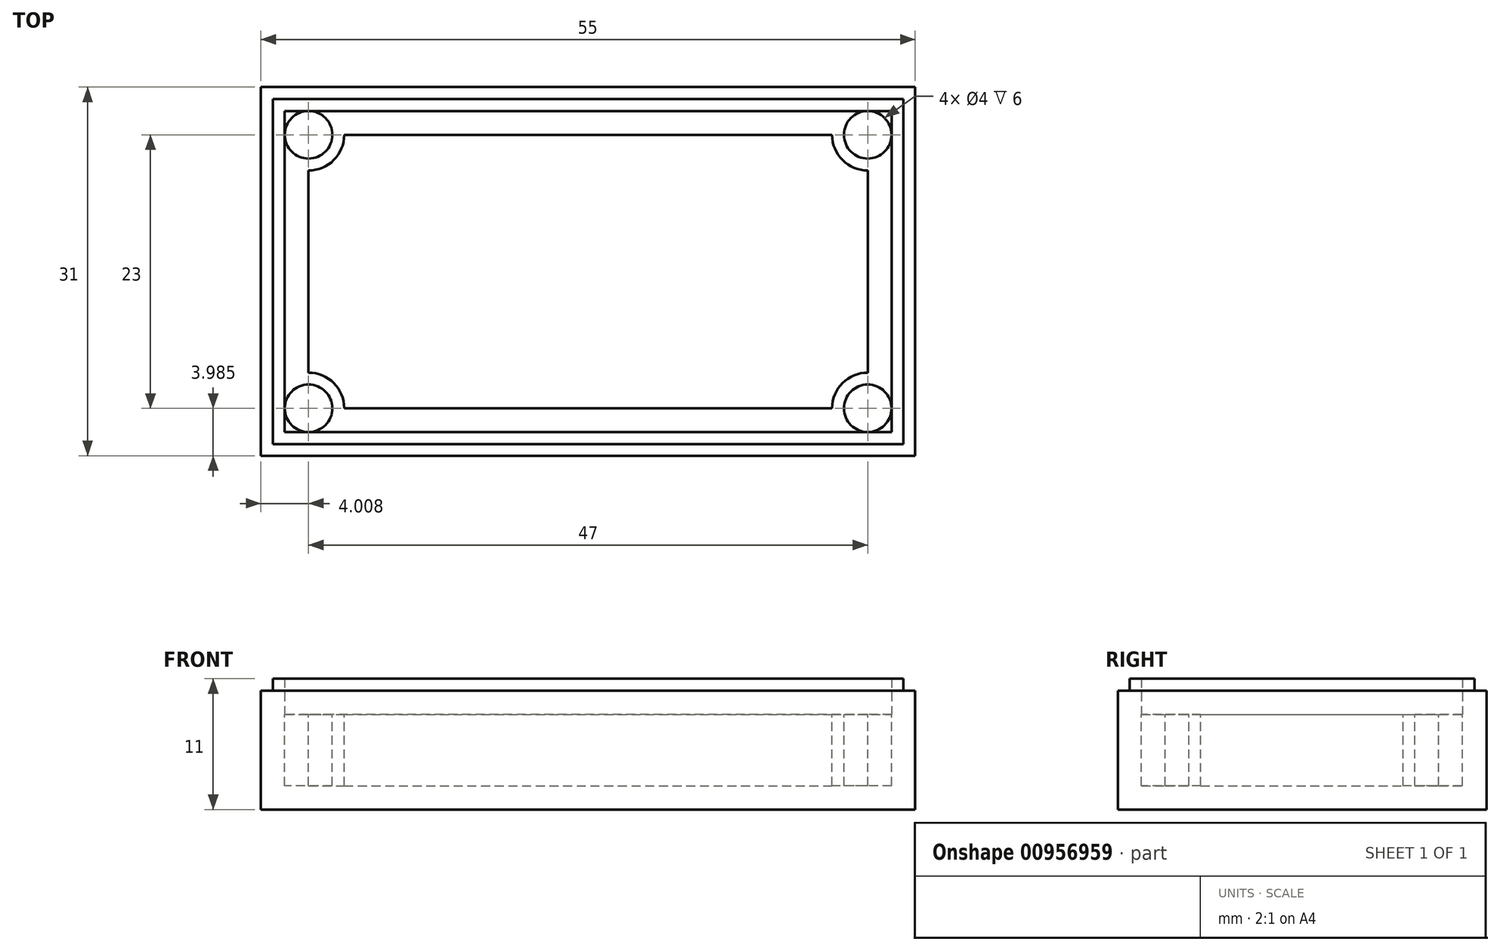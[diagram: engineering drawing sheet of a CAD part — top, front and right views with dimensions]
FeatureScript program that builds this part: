
annotation { "Feature Type Name" : "Feature", "Feature Type Description" : "" }
export const myFeature = defineFeature(function(context is Context, id is Id, definition is map)
    precondition{}
    {
        {
            var Q0;
            Q0=qCreatedBy(makeId("Top.planeOp"),FACE);
            var sketch = newSketch(context, id + "F0", { "sketchPlane" : qUnion([Q0])});
            skLineSegment(sketch, "E0.bottom", {"start": v(-24.52, 16.7) * mm, "end": v(30.48, 16.7) * mm});
            skLineSegment(sketch, "E0.top", {"start": v(-24.52, -14.3) * mm, "end": v(30.48, -14.3) * mm});
            skLineSegment(sketch, "E0.left", {"start": v(-24.52, 16.7) * mm, "end": v(-24.52, -14.3) * mm});
            skLineSegment(sketch, "E0.right", {"start": v(30.48, 16.7) * mm, "end": v(30.48, -14.3) * mm});
            skSolve(sketch);
        }
        {
            var Q0;
            Q0=makeQuery(id+"F0.imprint","IMPRINT",FACE,{"disambiguationData":[TD([[makeQuery(id+"F0.imprint","IMPRINT",EDGE,{"derivedFrom":sQuery(id+"F0.wireOp",EDGE,"E0.bottom")}),-1.0]])]});
            var sketch = newSketch(context, id + "F1", { "sketchPlane" : qUnion([Q0])});
            skLineSegment(sketch, "E1", {"start": v(-24.51, 15.7) * mm, "end": v(-23.51, 15.7) * mm});
            skLineSegment(sketch, "E2.bottom", {"start": v(-23.51, 15.7) * mm, "end": v(29.49, 15.7) * mm});
            skLineSegment(sketch, "E2.top", {"start": v(-23.51, -13.3) * mm, "end": v(29.49, -13.3) * mm});
            skLineSegment(sketch, "E2.left", {"start": v(-23.51, 15.7) * mm, "end": v(-23.51, -13.3) * mm});
            skLineSegment(sketch, "E2.right", {"start": v(29.49, 15.7) * mm, "end": v(29.49, -13.3) * mm});
            skLineSegment(sketch, "E3", {"start": v(-22.51, 15.7) * mm, "end": v(-22.51, 14.7) * mm});
            skLineSegment(sketch, "E4.bottom", {"start": v(-22.51, 14.7) * mm, "end": v(28.49, 14.7) * mm});
            skLineSegment(sketch, "E4.top", {"start": v(-22.51, -12.3) * mm, "end": v(28.49, -12.3) * mm});
            skLineSegment(sketch, "E4.left", {"start": v(-22.51, 14.7) * mm, "end": v(-22.51, -12.3) * mm});
            skLineSegment(sketch, "E4.right", {"start": v(28.49, 14.7) * mm, "end": v(28.49, -12.3) * mm});
            skSolve(sketch);
        }
        {
            var Q0;
            Q0 = qSketchRegion(id + "F0", true);
            extrude(context, id + "F2", {"entities" : qUnion([Q0]), "depth" : 10 * mm, "offsetDistance" : 25 * mm});
        }
        {
            var Q0;
            Q0=makeQuery(id+"F1.imprint","IMPRINT",FACE,{"disambiguationData":[TD([[makeQuery(id+"F1.imprint","IMPRINT",EDGE,{"derivedFrom":sQuery(id+"F1.wireOp",EDGE,"E2.top")}),1.0]])]});
            extrude(context, id + "F3", {"entities" : qUnion([Q0]), "operationType" : NewBodyOperationType.ADD, "depth" : 11 * mm, "offsetDistance" : 25 * mm});
        }
        {
            var Q0;
            Q0=makeQuery(id+"F3.boolean.opBoolean","SPLIT",FACE,{"disambiguationData":[TD([makeQuery(id+"F3.opExtrude","SWEPT_FACE",FACE,{"disambiguationData":[OSD([sQuery(id+"F1.wireOp",EDGE,"E4.bottom")])]})])],"derivedFrom":makeQuery(id+"F2.opExtrude","CAP_FACE",FACE,{"disambiguationData":[OSD([sQuery(id+"F0.wireOp",EDGE,"E0.bottom"),sQuery(id+"F0.wireOp",EDGE,"E0.top"),sQuery(id+"F0.wireOp",EDGE,"E0.left"),sQuery(id+"F0.wireOp",EDGE,"E0.right")])],"isStart":false})});
            extrude(context, id + "F4", {"entities" : qUnion([Q0]), "operationType" : NewBodyOperationType.REMOVE, "oppositeDirection" : true, "depth" : 8 * mm, "offsetDistance" : 25 * mm});
        }
        {
            var Q0;
            Q0=makeQuery(id+"F4.boolean.opBoolean","COPY",FACE,{"derivedFrom":makeQuery(id+"F4.opExtrude","CAP_FACE",FACE,{"disambiguationData":[OSD([sQuery(id+"F0.wireOp",EDGE,"E0.bottom"),sQuery(id+"F0.wireOp",EDGE,"E0.top"),sQuery(id+"F0.wireOp",EDGE,"E0.left"),sQuery(id+"F0.wireOp",EDGE,"E0.right")])],"isStart":false})});
            var sketch = newSketch(context, id + "F5", { "sketchPlane" : qUnion([Q0])});
            skLineSegment(sketch, "E5.bottom", {"start": v(-22.51, 14.7) * mm, "end": v(28.49, 14.7) * mm});
            skLineSegment(sketch, "E5.top", {"start": v(-22.51, 12.7) * mm, "end": v(28.49, 12.7) * mm});
            skLineSegment(sketch, "E5.left", {"start": v(-22.51, 14.7) * mm, "end": v(-22.51, 12.7) * mm});
            skLineSegment(sketch, "E5.right", {"start": v(28.49, 14.7) * mm, "end": v(28.49, 12.7) * mm});
            skLineSegment(sketch, "E6.bottom", {"start": v(-22.51, -12.3) * mm, "end": v(28.49, -12.3) * mm});
            skLineSegment(sketch, "E6.top", {"start": v(-22.51, -10.3) * mm, "end": v(28.49, -10.3) * mm});
            skLineSegment(sketch, "E6.left", {"start": v(-22.51, -12.3) * mm, "end": v(-22.51, -10.3) * mm});
            skLineSegment(sketch, "E6.right", {"start": v(28.49, -12.3) * mm, "end": v(28.49, -10.3) * mm});
            skSolve(sketch);
        }
        {
            var Q0;
            Q0=makeQuery(id+"F5.imprint","IMPRINT",FACE,{"disambiguationData":[TD([[makeQuery(id+"F5.imprint","IMPRINT",EDGE,{"derivedFrom":sQuery(id+"F5.wireOp",EDGE,"E5.bottom")}),1.0]])]});
            var Q1;
            Q1=makeQuery(id+"F5.imprint","IMPRINT",FACE,{"disambiguationData":[TD([[makeQuery(id+"F5.imprint","IMPRINT",EDGE,{"derivedFrom":sQuery(id+"F5.wireOp",EDGE,"E6.bottom")}),-1.0]])]});
            extrude(context, id + "F6", {"entities" : qUnion([Q0, Q1]), "operationType" : NewBodyOperationType.ADD, "depth" : 6 * mm, "offsetDistance" : 25 * mm});
        }
        {
            var Q0;
            Q0=makeQuery(id+"F4.boolean.opBoolean","COPY",FACE,{"derivedFrom":makeQuery(id+"F4.opExtrude","CAP_FACE",FACE,{"disambiguationData":[OSD([sQuery(id+"F0.wireOp",EDGE,"E0.bottom"),sQuery(id+"F0.wireOp",EDGE,"E0.top"),sQuery(id+"F0.wireOp",EDGE,"E0.left"),sQuery(id+"F0.wireOp",EDGE,"E0.right")])],"isStart":false})});
            var sketch = newSketch(context, id + "F7", { "sketchPlane" : qUnion([Q0])});
            skLineSegment(sketch, "E7", {"start": v(-22.51, 12.7) * mm, "end": v(-20.51, 12.7) * mm});
            skLineSegment(sketch, "E8", {"start": v(-20.51, 12.7) * mm, "end": v(-20.51, -10.3) * mm});
            skLineSegment(sketch, "E9", {"start": v(-20.51, -10.3) * mm, "end": v(26.49, -10.3) * mm});
            skLineSegment(sketch, "E10", {"start": v(26.49, -10.3) * mm, "end": v(26.49, 12.7) * mm});
            skSolve(sketch);
        }
        {
            var Q0;
            {var subQ0=sQuery(id+"F7.wireOp",EDGE,"E10");Q0=makeQuery(id+"F7.imprint","IMPRINT",FACE,{"disambiguationData":[TD([[makeQuery(id+"F7.imprint","IMPRINT",EDGE,{"derivedFrom":subQ0}),-1.0]])]});}
            var Q1;
            Q1=makeQuery(id+"F7.imprint","IMPRINT",FACE,{"disambiguationData":[TD([[makeQuery(id+"F7.imprint","IMPRINT",EDGE,{"derivedFrom":sQuery(id+"F7.wireOp",EDGE,"E7")}),-1.0]])]});
            extrude(context, id + "F8", {"entities" : qUnion([Q0, Q1]), "operationType" : NewBodyOperationType.ADD, "depth" : 6 * mm, "offsetDistance" : 25 * mm});
        }
        {
            var Q0;
            {var subQ0=sQuery(id+"F5.wireOp",EDGE,"E6.top");var subQ1=sQuery(id+"F5.wireOp",EDGE,"E5.top");var subQ2=sQuery(id+"F0.wireOp",EDGE,"E0.right");var subQ3=sQuery(id+"F0.wireOp",EDGE,"E0.left");var subQ4=sQuery(id+"F0.wireOp",EDGE,"E0.top");var subQ5=sQuery(id+"F0.wireOp",EDGE,"E0.bottom");Q0=makeQuery(id+"F8.boolean.opBoolean","MERGE",FACE,{"derivedFrom":[makeQuery(id+"F6.opExtrude","CAP_FACE",FACE,{"disambiguationData":[OSD([sQuery(id+"F5.wireOp",EDGE,"E5.bottom"),subQ1,sQuery(id+"F5.wireOp",EDGE,"E5.left"),sQuery(id+"F5.wireOp",EDGE,"E5.right")])],"isStart":false}),makeQuery(id+"F6.opExtrude","CAP_FACE",FACE,{"disambiguationData":[OSD([sQuery(id+"F5.wireOp",EDGE,"E6.bottom"),subQ0,sQuery(id+"F5.wireOp",EDGE,"E6.left"),sQuery(id+"F5.wireOp",EDGE,"E6.right")])],"isStart":false}),makeQuery(id+"F8.opExtrude","CAP_FACE",FACE,{"disambiguationData":[OSD([subQ5,subQ4,subQ3,subQ2,sQuery(id+"F1.wireOp",EDGE,"E4.left"),subQ0,sQuery(id+"F7.wireOp",EDGE,"E7"),sQuery(id+"F7.wireOp",EDGE,"E8")])],"isStart":false}),makeQuery(id+"F8.opExtrude","CAP_FACE",FACE,{"disambiguationData":[OSD([subQ5,subQ4,subQ3,subQ2,sQuery(id+"F1.wireOp",EDGE,"E4.right"),subQ1,subQ0,sQuery(id+"F7.wireOp",EDGE,"E10")])],"isStart":false})]});}
            var sketch = newSketch(context, id + "F9", { "sketchPlane" : qUnion([Q0])});
            skCircle(sketch, "E11", {"center": v(-20.51, 12.7) * mm, "radius": 3 * mm});
            skCircle(sketch, "E12", {"center": v(-20.51, 12.7) * mm, "radius": 2 * mm});
            skCircle(sketch, "E13", {"center": v(-20.51, -10.3) * mm, "radius": 3 * mm});
            skCircle(sketch, "E14", {"center": v(-20.51, -10.3) * mm, "radius": 2 * mm});
            skCircle(sketch, "E15", {"center": v(26.49, 12.7) * mm, "radius": 3 * mm});
            skCircle(sketch, "E16", {"center": v(26.49, 12.7) * mm, "radius": 2 * mm});
            skCircle(sketch, "E17", {"center": v(26.49, -10.3) * mm, "radius": 3 * mm});
            skCircle(sketch, "E18", {"center": v(26.49, -10.3) * mm, "radius": 2 * mm});
            skSolve(sketch);
        }
        {
            var Q0;
            {var subQ0=sQuery(id+"F9.wireOp",EDGE,"E11");var subQ1=makeQuery(id+"F6.opExtrude","CAP_EDGE",EDGE,{"disambiguationData":[OSD([sQuery(id+"F5.wireOp",EDGE,"E5.top")])],"isStart":false});var subQ2=makeQuery(id+"F9.imprint","INTERSECT",VERTEX,{"derivedFrom":[subQ1,subQ0]});Q0=makeQuery(id+"F9.imprint","IMPRINT",FACE,{"disambiguationData":[TD([[makeQuery(id+"F9.imprint","IMPRINT",EDGE,{"disambiguationData":[TD([[subQ2,1.0]])],"derivedFrom":subQ0}),1.0]])]});}
            var Q1;
            {var subQ0=sQuery(id+"F9.wireOp",EDGE,"E13");var subQ1=makeQuery(id+"F8.opExtrude","CAP_EDGE",EDGE,{"disambiguationData":[OSD([sQuery(id+"F7.wireOp",EDGE,"E8")])],"isStart":false});var subQ2=makeQuery(id+"F9.imprint","INTERSECT",VERTEX,{"derivedFrom":[subQ1,subQ0]});Q1=makeQuery(id+"F9.imprint","IMPRINT",FACE,{"disambiguationData":[TD([[makeQuery(id+"F9.imprint","IMPRINT",EDGE,{"disambiguationData":[TD([[subQ2,1.0]])],"derivedFrom":subQ0}),1.0]])]});}
            var Q2;
            {var subQ0=sQuery(id+"F9.wireOp",EDGE,"E17");var subQ1=makeQuery(id+"F8.opExtrude","CAP_EDGE",EDGE,{"disambiguationData":[OSD([sQuery(id+"F7.wireOp",EDGE,"E10")])],"isStart":false});var subQ2=makeQuery(id+"F9.imprint","INTERSECT",VERTEX,{"derivedFrom":[subQ1,subQ0]});Q2=makeQuery(id+"F9.imprint","IMPRINT",FACE,{"disambiguationData":[TD([[makeQuery(id+"F9.imprint","IMPRINT",EDGE,{"disambiguationData":[TD([[subQ2,-1.0]])],"derivedFrom":subQ0}),1.0]])]});}
            var Q3;
            {var subQ0=sQuery(id+"F9.wireOp",EDGE,"E15");var subQ1=makeQuery(id+"F6.opExtrude","CAP_EDGE",EDGE,{"disambiguationData":[OSD([sQuery(id+"F5.wireOp",EDGE,"E5.top")])],"isStart":false});var subQ2=makeQuery(id+"F9.imprint","INTERSECT",VERTEX,{"derivedFrom":[subQ1,subQ0]});Q3=makeQuery(id+"F9.imprint","IMPRINT",FACE,{"disambiguationData":[TD([[makeQuery(id+"F9.imprint","IMPRINT",EDGE,{"disambiguationData":[TD([[subQ2,-1.0]])],"derivedFrom":subQ0}),1.0]])]});}
            extrude(context, id + "F10", {"entities" : qUnion([Q0, Q1, Q2, Q3]), "operationType" : NewBodyOperationType.ADD, "depth" : -6 * mm, "offsetDistance" : 25 * mm});
        }
        {
            var Q0;
            {var subQ3=sQuery(id+"F9.wireOp",EDGE,"E12");var subQ5=makeQuery(id+"F9.imprint","INTERSECT",VERTEX,{"derivedFrom":[makeQuery(id+"F6.opExtrude","CAP_EDGE",EDGE,{"disambiguationData":[OSD([sQuery(id+"F5.wireOp",EDGE,"E5.bottom")])],"isStart":false}),subQ3]});Q0=makeQuery(id+"F9.imprint","IMPRINT",FACE,{"disambiguationData":[TD([[makeQuery(id+"F9.imprint","IMPRINT",EDGE,{"disambiguationData":[TD([[subQ5,1.0]])],"derivedFrom":subQ3}),1.0]])]});}
            var Q1;
            {var subQ0=sQuery(id+"F9.wireOp",EDGE,"E14");var subQ1=makeQuery(id+"F6.opExtrude","CAP_EDGE",EDGE,{"disambiguationData":[OSD([sQuery(id+"F5.wireOp",EDGE,"E6.top")])],"isStart":false});var subQ2=makeQuery(id+"F9.imprint","INTERSECT",VERTEX,{"derivedFrom":[subQ1,subQ0]});Q1=makeQuery(id+"F9.imprint","IMPRINT",FACE,{"disambiguationData":[TD([[makeQuery(id+"F9.imprint","IMPRINT",EDGE,{"disambiguationData":[TD([[subQ2,1.0]])],"derivedFrom":subQ0}),1.0]])]});}
            var Q2;
            {var subQ0=sQuery(id+"F9.wireOp",EDGE,"E18");var subQ3=makeQuery(id+"F6.opExtrude","CAP_EDGE",EDGE,{"disambiguationData":[OSD([sQuery(id+"F5.wireOp",EDGE,"E6.top")])],"isStart":false});var subQ7=makeQuery(id+"F9.imprint","INTERSECT",VERTEX,{"derivedFrom":[subQ3,subQ0]});Q2=makeQuery(id+"F9.imprint","IMPRINT",FACE,{"disambiguationData":[TD([[makeQuery(id+"F9.imprint","IMPRINT",EDGE,{"disambiguationData":[TD([[subQ7,-1.0]])],"derivedFrom":subQ0}),1.0]])]});}
            var Q3;
            {var subQ0=sQuery(id+"F9.wireOp",EDGE,"E16");var subQ6=makeQuery(id+"F9.imprint","INTERSECT",VERTEX,{"derivedFrom":[makeQuery(id+"F6.opExtrude","CAP_EDGE",EDGE,{"disambiguationData":[OSD([sQuery(id+"F5.wireOp",EDGE,"E5.bottom")])],"isStart":false}),subQ0]});Q3=makeQuery(id+"F9.imprint","IMPRINT",FACE,{"disambiguationData":[TD([[makeQuery(id+"F9.imprint","IMPRINT",EDGE,{"disambiguationData":[TD([[subQ6,-1.0]])],"derivedFrom":subQ0}),1.0]])]});}
            extrude(context, id + "F11", {"entities" : qUnion([Q0, Q1, Q2, Q3]), "operationType" : NewBodyOperationType.REMOVE, "oppositeDirection" : true, "depth" : 6 * mm, "offsetDistance" : 25 * mm});
        }
    });
